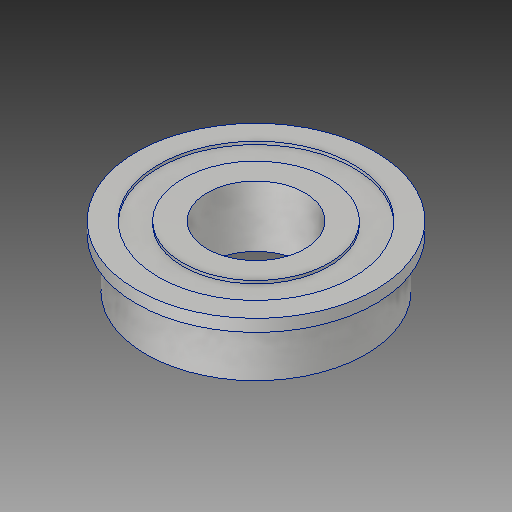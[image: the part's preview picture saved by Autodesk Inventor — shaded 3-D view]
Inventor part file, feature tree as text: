
AUTODESK INVENTOR PART (.ipt)
format: ipt  version: 2017 (Build 210142000, 142)  size: 124,928 bytes
history: native  units: in
note: dims shown in document units (in); Inventor stores cm internally (conversion verified against a paired STEP export)
features: revolve x1
ambient origin geometry x8: Origin, YZ Plane, XZ Plane, XY Plane, X Axis, Y Axis, Z Axis, Center Point
bodies: Solid1 (feature_tree)
feature tree (1):
  revolve  "Revolve1"  [1 undecoded]
note: 1 required parameter value undecoded (feature->parameter linkage not recoverable at this tier; creation-order binding heuristic only, values carry confidence <= 0.55)
